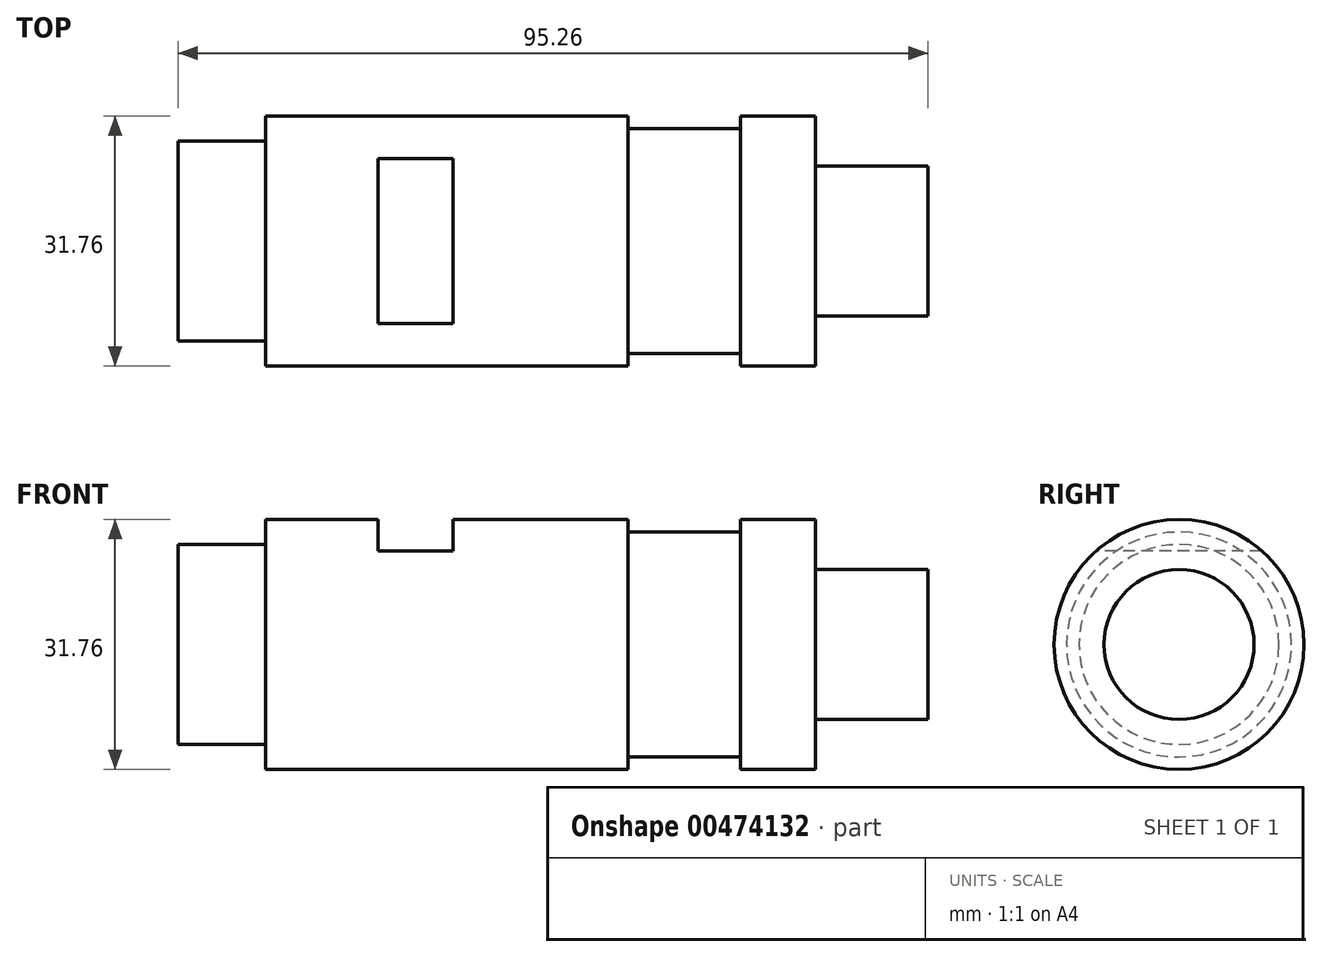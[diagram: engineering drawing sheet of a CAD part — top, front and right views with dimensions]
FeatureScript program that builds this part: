
annotation { "Feature Type Name" : "Feature", "Feature Type Description" : "" }
export const myFeature = defineFeature(function(context is Context, id is Id, definition is map)
    precondition{}
    {
        {
            var Q0;
            Q0=qCreatedBy(makeId("Front.planeOp"),FACE);
            var sketch = newSketch(context, id + "F0", { "sketchPlane" : qUnion([Q0])});
            skLineSegment(sketch, "E0", {"start": v(-47.63, 0) * mm, "end": v(47.63, 0) * mm});
            skLineSegment(sketch, "E1", {"start": v(-47.63, 0) * mm, "end": v(-47.63, 12.7) * mm});
            skLineSegment(sketch, "E2", {"start": v(-47.63, 12.7) * mm, "end": v(-36.51, 12.7) * mm});
            skLineSegment(sketch, "E3", {"start": v(-36.51, 12.7) * mm, "end": v(-36.51, 0) * mm});
            skLineSegment(sketch, "E4", {"start": v(-36.51, 0) * mm, "end": v(9.54, 0) * mm});
            skLineSegment(sketch, "E5", {"start": v(9.54, 0) * mm, "end": v(9.54, 14.29) * mm});
            skLineSegment(sketch, "E6", {"start": v(9.54, 14.29) * mm, "end": v(23.83, 14.29) * mm});
            skLineSegment(sketch, "E7", {"start": v(23.83, 14.29) * mm, "end": v(23.83, 0) * mm});
            skLineSegment(sketch, "E8", {"start": v(23.83, 0) * mm, "end": v(33.34, 0) * mm});
            skLineSegment(sketch, "E9", {"start": v(33.34, 0) * mm, "end": v(33.34, 15.87) * mm});
            skLineSegment(sketch, "E10", {"start": v(33.34, 15.87) * mm, "end": v(23.81, 15.87) * mm});
            skLineSegment(sketch, "E11", {"start": v(23.81, 15.87) * mm, "end": v(23.83, 14.29) * mm});
            skLineSegment(sketch, "E12", {"start": v(47.63, 0) * mm, "end": v(47.63, 9.53) * mm});
            skLineSegment(sketch, "E13", {"start": v(47.62, 9.53) * mm, "end": v(33.34, 9.53) * mm});
            skLineSegment(sketch, "E14", {"start": v(-36.51, 15.87) * mm, "end": v(9.54, 15.88) * mm});
            skLineSegment(sketch, "E15", {"start": v(-36.51, 15.87) * mm, "end": v(-36.51, 0) * mm});
            skLineSegment(sketch, "E16", {"start": v(9.54, 15.88) * mm, "end": v(9.54, 0) * mm});
            skSolve(sketch);
        }
        {
            var Q0;
            Q0 = qSketchRegion(id + "F0", true);
            var Q1;
            Q1=sQuery(id+"F0.wireOp",EDGE,"E0");
            revolve(context, id + "F1", {"entities" : qUnion([Q0]), "axis" : qUnion([Q1]), "revolveType" : RevolveType.FULL});
        }
        {
            var Q0;
            Q0=qCreatedBy(makeId("Front.planeOp"),FACE);
            var sketch = newSketch(context, id + "F2", { "sketchPlane" : qUnion([Q0])});
            skLineSegment(sketch, "E17.bottom", {"start": v(-22.23, 11.9) * mm, "end": v(-12.69, 11.9) * mm});
            skLineSegment(sketch, "E17.top", {"start": v(-22.23, 35.61) * mm, "end": v(-12.69, 35.61) * mm});
            skLineSegment(sketch, "E17.left", {"start": v(-22.22, 11.9) * mm, "end": v(-22.23, 35.61) * mm});
            skLineSegment(sketch, "E17.right", {"start": v(-12.69, 11.9) * mm, "end": v(-12.69, 35.61) * mm});
            skSolve(sketch);
        }
        {
            var Q0;
            Q0 = qSketchRegion(id + "F2", true);
            extrude(context, id + "F3", {"entities" : qUnion([Q0]), "operationType" : NewBodyOperationType.REMOVE, "endBound" : BoundingType.SYMMETRIC, "oppositeDirection" : true, "depth" : 127 * mm});
        }
    });
